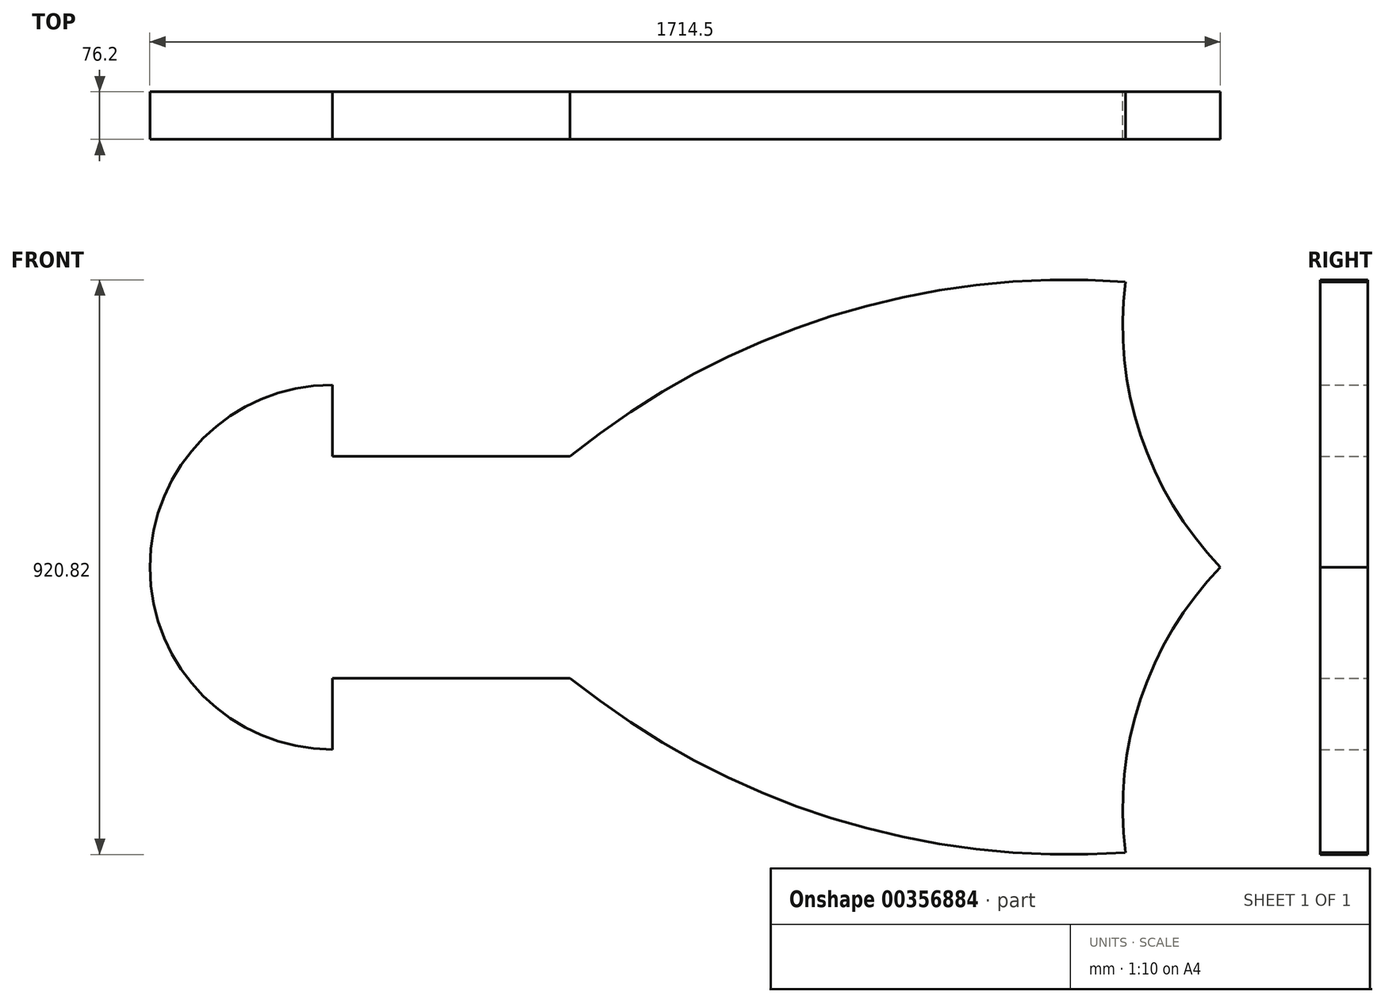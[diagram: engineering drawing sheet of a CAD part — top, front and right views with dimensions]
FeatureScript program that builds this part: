
annotation { "Feature Type Name" : "Feature", "Feature Type Description" : "" }
export const myFeature = defineFeature(function(context is Context, id is Id, definition is map)
    precondition{}
    {
        {
            var Q0;
            Q0=qCreatedBy(makeId("Front.planeOp"),FACE);
            var sketch = newSketch(context, id + "F0", { "sketchPlane" : qUnion([Q0])});
            skLineSegment(sketch, "E0", {"start": v(-1370.78, 0) * mm, "end": v(983.8, 0) * mm, "construction": true});
            skArc(sketch, "E1", {"start": v(-940.2, 292.1) * mm, "mid": v(-1146.74, 206.55) * mm, "end": v(-1232.3, 0) * mm});
            skLineSegment(sketch, "E2", {"start": v(-940.2, 177.8) * mm, "end": v(-559.2, 177.8) * mm});
            skLineSegment(sketch, "E3.trimOffspring", {"start": v(-940.2, 177.8) * mm, "end": v(-940.2, 292.1) * mm});
            skLineSegment(sketch, "E4", {"start": v(202.9, 457.2) * mm, "end": v(482.08, 457.2) * mm, "construction": true});
            skLineSegment(sketch, "E5", {"start": v(329.8, 519.2) * mm, "end": v(329.8, 229.47) * mm, "construction": true});
            skLineSegment(sketch, "E6", {"start": v(482.2, 142.76) * mm, "end": v(482.2, -178.7) * mm, "construction": true});
            skArc(sketch, "E7", {"start": v(329.8, 457.2) * mm, "mid": v(-141.25, 401.98) * mm, "end": v(-559.2, 177.8) * mm});
            skArc(sketch, "E8", {"start": v(329.8, 457.2) * mm, "mid": v(354.18, 211.33) * mm, "end": v(482.2, 0) * mm});
            skArc(sketch, "E9.MirrorCS", {"start": v(-940.2, -292.1) * mm, "mid": v(-1146.74, -206.55) * mm, "end": v(-1232.3, 0) * mm});
            skLineSegment(sketch, "E10.MirrorCS", {"start": v(-940.2, -177.8) * mm, "end": v(-559.2, -177.8) * mm});
            skLineSegment(sketch, "E11.MirrorCS", {"start": v(202.9, -457.2) * mm, "end": v(482.08, -457.2) * mm, "construction": true});
            skArc(sketch, "E12.MirrorCS", {"start": v(329.8, -457.2) * mm, "mid": v(354.18, -211.33) * mm, "end": v(482.2, 0) * mm});
            skArc(sketch, "E13.MirrorCS", {"start": v(329.8, -457.2) * mm, "mid": v(-141.25, -401.98) * mm, "end": v(-559.2, -177.8) * mm});
            skLineSegment(sketch, "E14.MirrorCS", {"start": v(482.2, -142.76) * mm, "end": v(482.2, 178.7) * mm, "construction": true});
            skLineSegment(sketch, "E15.MirrorCS", {"start": v(329.8, -519.2) * mm, "end": v(329.8, -229.47) * mm, "construction": true});
            skLineSegment(sketch, "E16.MirrorCS", {"start": v(-940.2, -177.8) * mm, "end": v(-940.2, -292.1) * mm});
            skSolve(sketch);
        }
        {
            var Q0;
            Q0 = qSketchRegion(id + "F0", true);
            extrude(context, id + "F1", {"entities" : qUnion([Q0]), "depth" : 76.2 * mm});
        }
    });
